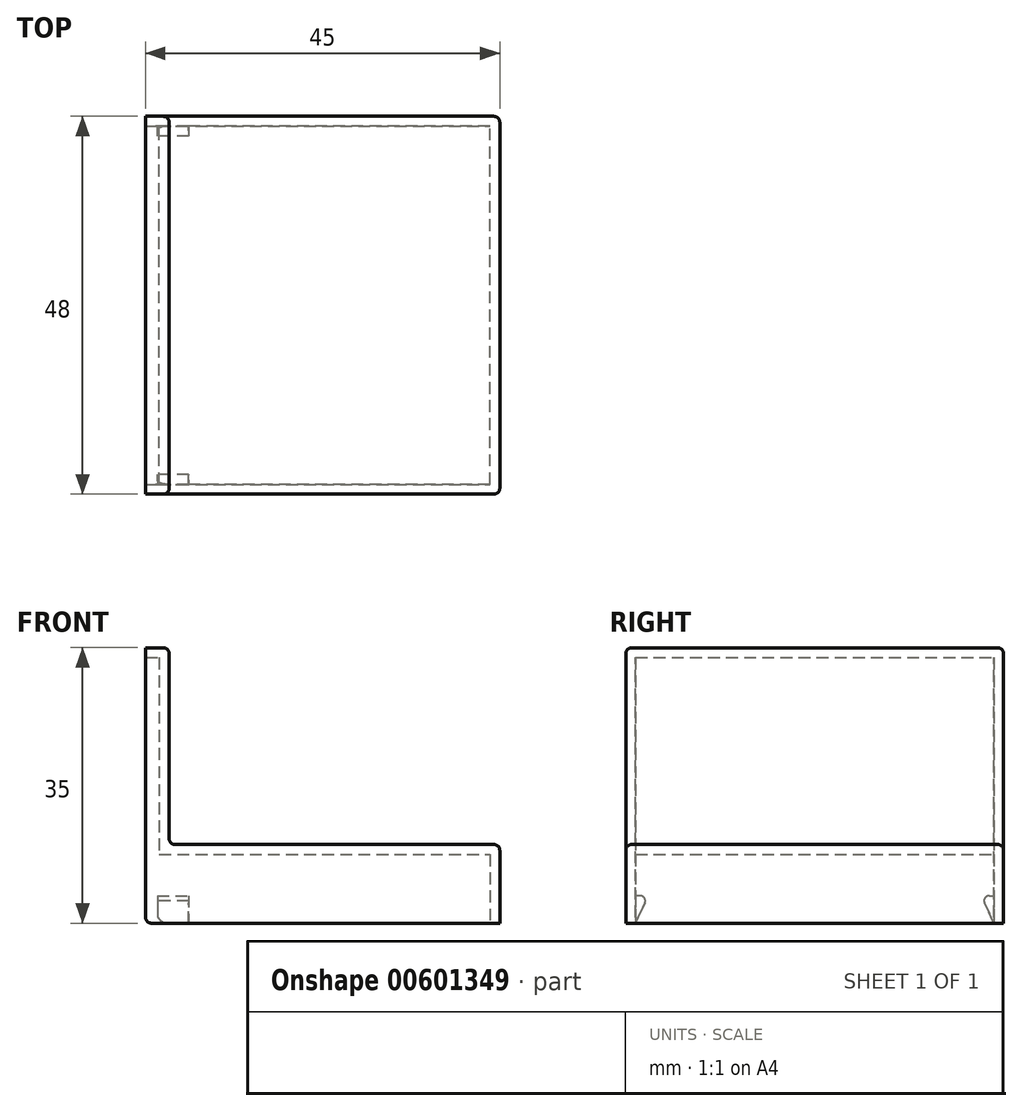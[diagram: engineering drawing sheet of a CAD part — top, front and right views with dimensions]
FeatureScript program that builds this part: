
annotation { "Feature Type Name" : "Feature", "Feature Type Description" : "" }
export const myFeature = defineFeature(function(context is Context, id is Id, definition is map)
    precondition{}
    {
        {
            var Q0;
            Q0=qCreatedBy(makeId("Front.planeOp"),FACE);
            var sketch = newSketch(context, id + "F0", { "sketchPlane" : qUnion([Q0])});
            skLineSegment(sketch, "E0", {"start": v(-44.9, -20.02) * mm, "end": v(-44.9, 14.98) * mm});
            skLineSegment(sketch, "E1", {"start": v(-44.9, 14.98) * mm, "end": v(-41.9, 14.98) * mm});
            skLineSegment(sketch, "E2", {"start": v(-41.9, 14.98) * mm, "end": v(-41.9, -10.02) * mm});
            skLineSegment(sketch, "E3", {"start": v(-41.9, -10.02) * mm, "end": v(0.1, -10.02) * mm});
            skLineSegment(sketch, "E4", {"start": v(0.1, -10.02) * mm, "end": v(0.1, -20.02) * mm});
            skLineSegment(sketch, "E5", {"start": v(0.1, -20.02) * mm, "end": v(-44.9, -20.02) * mm});
            skSolve(sketch);
        }
        {
            var Q0;
            Q0=makeQuery(id+"F0.imprint","IMPRINT",FACE,{"disambiguationData":[TD([[makeQuery(id+"F0.imprint","IMPRINT",EDGE,{"derivedFrom":sQuery(id+"F0.wireOp",EDGE,"E0")}),-1.0]])]});
            extrude(context, id + "F1", {"entities" : qUnion([Q0]), "depth" : 48 * mm});
        }
        {
            var Q0;
            Q0=makeQuery(id+"F1.opExtrude","SWEPT_FACE",FACE,{"disambiguationData":[OSD([sQuery(id+"F0.wireOp",EDGE,"E0")])]});
            var Q1;
            Q1=makeQuery(id+"F1.opExtrude","SWEPT_FACE",FACE,{"disambiguationData":[OSD([sQuery(id+"F0.wireOp",EDGE,"E5")])]});
            shell(context, id + "F2", {"entities" : qUnion([Q0, Q1]), "thickness" : 1.25 * mm});
        }
        {
            var Q0;
            Q0=makeQuery(id+"F1.opExtrude","CAP_EDGE",EDGE,{"disambiguationData":[OSD([sQuery(id+"F0.wireOp",EDGE,"E4")])],"isStart":false});
            var Q1;
            Q1=makeQuery(id+"F1.opExtrude","SWEPT_EDGE",EDGE,{"disambiguationData":[OSD([sQuery(id+"F0.wireOp",EDGE,"E3"),sQuery(id+"F0.wireOp",EDGE,"E4")])]});
            var Q2;
            Q2=makeQuery(id+"F1.opExtrude","CAP_EDGE",EDGE,{"disambiguationData":[OSD([sQuery(id+"F0.wireOp",EDGE,"E4")])],"isStart":true});
            var Q3;
            Q3=makeQuery(id+"F1.opExtrude","CAP_EDGE",EDGE,{"disambiguationData":[OSD([sQuery(id+"F0.wireOp",EDGE,"E3")])],"isStart":true});
            var Q4;
            Q4=makeQuery(id+"F1.opExtrude","SWEPT_FACE",FACE,{"disambiguationData":[OSD([sQuery(id+"F0.wireOp",EDGE,"E3")])]});
            var Q5;
            Q5=makeQuery(id+"F1.opExtrude","SWEPT_FACE",FACE,{"disambiguationData":[OSD([sQuery(id+"F0.wireOp",EDGE,"E2")])]});
            var Q6;
            Q6=makeQuery(id+"F1.opExtrude","CAP_EDGE",EDGE,{"disambiguationData":[OSD([sQuery(id+"F0.wireOp",EDGE,"E3")])],"isStart":false});
            var Q7;
            Q7=makeQuery(id+"F1.opExtrude","CAP_EDGE",EDGE,{"disambiguationData":[OSD([sQuery(id+"F0.wireOp",EDGE,"E2")])],"isStart":false});
            var Q8;
            Q8=makeQuery(id+"F1.opExtrude","CAP_EDGE",EDGE,{"disambiguationData":[OSD([sQuery(id+"F0.wireOp",EDGE,"E1")])],"isStart":false});
            var Q9;
            Q9=makeQuery(id+"F1.opExtrude","CAP_EDGE",EDGE,{"disambiguationData":[OSD([sQuery(id+"F0.wireOp",EDGE,"E1")])],"isStart":true});
            var Q10;
            Q10=makeQuery(id+"F1.opExtrude","SWEPT_EDGE",EDGE,{"disambiguationData":[OSD([sQuery(id+"F0.wireOp",EDGE,"E0"),sQuery(id+"F0.wireOp",EDGE,"E5")])]});
            var Q11;
            Q11=makeQuery(id+"F2.opShell","OFFSET_EDGE",EDGE,{"disambiguationData":[OSD([sQuery(id+"F0.wireOp",EDGE,"E0"),sQuery(id+"F0.wireOp",EDGE,"E5")])]});
            fillet(context, id + "F3", {"entities" : qUnion([Q0, Q1, Q2, Q3, Q4, Q5, Q6, Q7, Q8, Q9, Q10, Q11]), "radius" : 0.75 * mm, "tangentPropagation" : true, "allowEdgeOverflow" : false});
        }
        {
            var Q0;
            {var subQ0=sQuery(id+"F0.wireOp",EDGE,"E0");var subQ1=sQuery(id+"F0.wireOp",EDGE,"E1");var subQ2=sQuery(id+"F0.wireOp",EDGE,"E2");var subQ3=sQuery(id+"F0.wireOp",EDGE,"E3");var subQ4=sQuery(id+"F0.wireOp",EDGE,"E4");var subQ5=sQuery(id+"F0.wireOp",EDGE,"E5");Q0=makeQuery(id+"F2.opShell","OFFSET_FACE",FACE,{"disambiguationData":[OSD([subQ0,subQ1,subQ2,subQ3,subQ4,subQ5]),TDD([makeQuery(id+"F1.opExtrude","CAP_FACE",FACE,{"disambiguationData":[OSD([subQ0,subQ1,subQ2,subQ3,subQ4,subQ5])],"isStart":true})])]});}
            var sketch = newSketch(context, id + "F4", { "sketchPlane" : qUnion([Q0])});
            skLineSegment(sketch, "E6.bottom", {"start": v(-43.4, -16.52) * mm, "end": v(-39.4, -16.52) * mm});
            skLineSegment(sketch, "E6.top", {"start": v(-43.4, -20.02) * mm, "end": v(-39.4, -20.02) * mm});
            skLineSegment(sketch, "E6.left", {"start": v(-43.4, -16.52) * mm, "end": v(-43.4, -20.02) * mm});
            skLineSegment(sketch, "E6.right", {"start": v(-39.4, -16.52) * mm, "end": v(-39.4, -20.02) * mm});
            skSolve(sketch);
        }
        {
            var Q0;
            Q0=qSketchRegion(id+"F4",true);
            extrude(context, id + "F5", {"entities" : qUnion([Q0]), "operationType" : NewBodyOperationType.ADD, "depth" : 1.25 * mm});
        }
        {
            var Q0;
            Q0=makeQuery(id+"F5.opExtrude","SWEPT_EDGE",EDGE,{"disambiguationData":[OSD([sQuery(id+"F0.wireOp",EDGE,"E5"),sQuery(id+"F4.wireOp",EDGE,"E6.top"),sQuery(id+"F4.wireOp",EDGE,"E6.left")])]});
            fillet(context, id + "F6", {"entities" : qUnion([Q0]), "radius" : 1.25 * mm, "tangentPropagation" : true, "allowEdgeOverflow" : false});
        }
        {
            var Q0;
            Q0=makeQuery(id+"F5.opExtrude","CAP_EDGE",EDGE,{"disambiguationData":[OSD([sQuery(id+"F4.wireOp",EDGE,"E6.top")])],"isStart":false});
            chamfer(context, id + "F7", {"entities" : qUnion([Q0]), "chamferType" : ChamferType.TWO_OFFSETS, "width1" : 1.25 * mm, "oppositeDirection" : false, "width2" : 2.75 * mm});
        }
        {
            var Q0;
            {var subQ0=sQuery(id+"F4.wireOp",EDGE,"E6.top");Q0=makeQuery(id+"F7.opChamfer","BLEND_EDGE",EDGE,{"blendedFrom":[makeQuery(id+"F5.opExtrude","CAP_EDGE",EDGE,{"disambiguationData":[OSD([subQ0])],"isStart":false}),makeQuery(id+"F5.opExtrude","CAP_FACE",FACE,{"disambiguationData":[OSD([sQuery(id+"F4.wireOp",EDGE,"E6.bottom"),subQ0,sQuery(id+"F4.wireOp",EDGE,"E6.left"),sQuery(id+"F4.wireOp",EDGE,"E6.right")])],"isStart":false})],"blendedInto":[makeQuery(id+"F5.opExtrude","CAP_FACE",FACE,{"disambiguationData":[OSD([sQuery(id+"F4.wireOp",EDGE,"E6.bottom"),subQ0,sQuery(id+"F4.wireOp",EDGE,"E6.left"),sQuery(id+"F4.wireOp",EDGE,"E6.right")])],"isStart":false})]});}
            var Q1;
            Q1=makeQuery(id+"F5.opExtrude","CAP_EDGE",EDGE,{"disambiguationData":[OSD([sQuery(id+"F4.wireOp",EDGE,"E6.bottom")])],"isStart":false});
            fillet(context, id + "F8", {"entities" : qUnion([Q0, Q1]), "radius" : 0.7 * mm, "tangentPropagation" : true, "allowEdgeOverflow" : false});
        }
        {
            var Q0;
            Q0=makeQuery(id+"F1.opExtrude","SWEPT_BODY",BODY,{"disambiguationData":[OSD([sQuery(id+"F0.wireOp",EDGE,"E0"),sQuery(id+"F0.wireOp",EDGE,"E1"),sQuery(id+"F0.wireOp",EDGE,"E2"),sQuery(id+"F0.wireOp",EDGE,"E3"),sQuery(id+"F0.wireOp",EDGE,"E4"),sQuery(id+"F0.wireOp",EDGE,"E5")])]});
            transform(context, id + "F9", {"entities" : qUnion([Q0]), "transformType" : TransformType.TRANSLATION_3D, "dx" : 0 * mm, "dy" : 24 * mm, "dz" : 0 * mm, "makeCopy" : false});
        }
        {
            var Q0;
            Q0=makeQuery(id+"F1.opExtrude","SWEPT_BODY",BODY,{"disambiguationData":[OSD([sQuery(id+"F0.wireOp",EDGE,"E0"),sQuery(id+"F0.wireOp",EDGE,"E1"),sQuery(id+"F0.wireOp",EDGE,"E2"),sQuery(id+"F0.wireOp",EDGE,"E3"),sQuery(id+"F0.wireOp",EDGE,"E4"),sQuery(id+"F0.wireOp",EDGE,"E5")])]});
            var Q1;
            Q1=qCreatedBy(makeId("Front.planeOp"),FACE);
            mirror(context, id + "F10", {"operationType" : NewBodyOperationType.ADD, "entities" : qUnion([Q0]), "mirrorPlane" : qUnion([Q1])});
        }
    });
